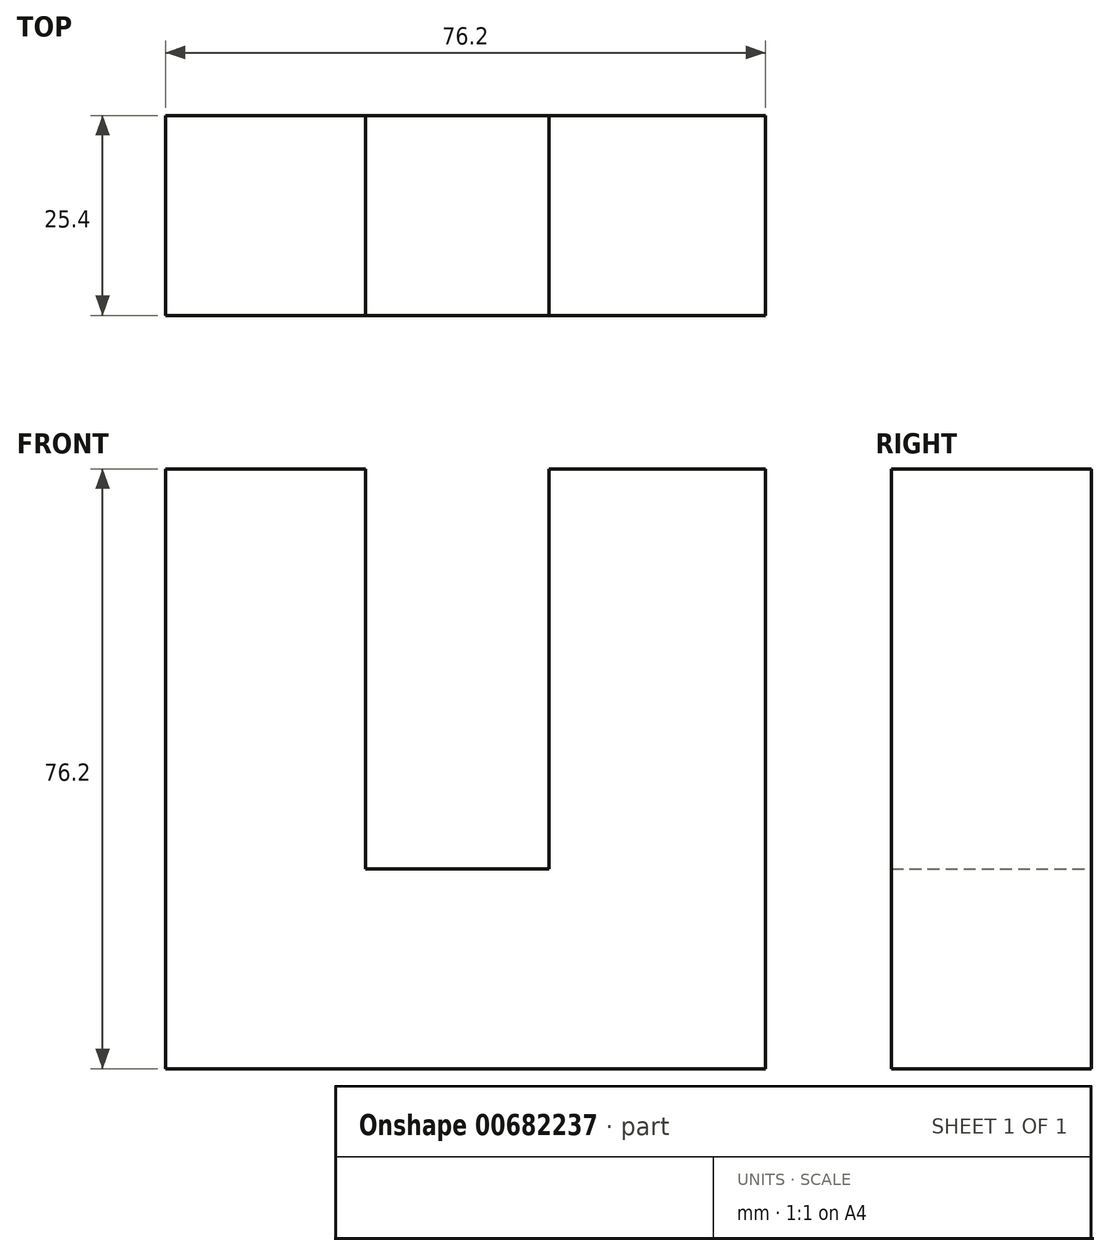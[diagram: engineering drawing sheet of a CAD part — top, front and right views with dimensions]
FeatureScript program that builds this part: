
annotation { "Feature Type Name" : "Feature", "Feature Type Description" : "" }
export const myFeature = defineFeature(function(context is Context, id is Id, definition is map)
    precondition{}
    {
        {
            var Q0;
            Q0=qCreatedBy(makeId("Front.planeOp"),FACE);
            var sketch = newSketch(context, id + "F0", { "sketchPlane" : qUnion([Q0])});
            skLineSegment(sketch, "E0", {"start": v(0, 0) * mm, "end": v(-76.2, 0) * mm});
            skLineSegment(sketch, "E1", {"start": v(-76.2, 0) * mm, "end": v(-76.2, 76.2) * mm});
            skLineSegment(sketch, "E2", {"start": v(-76.2, 76.2) * mm, "end": v(-50.8, 76.2) * mm});
            skLineSegment(sketch, "E3", {"start": v(-50.8, 76.2) * mm, "end": v(-50.8, 25.4) * mm});
            skLineSegment(sketch, "E4", {"start": v(-50.8, 25.4) * mm, "end": v(-27.49, 25.4) * mm});
            skLineSegment(sketch, "E5", {"start": v(-27.49, 25.4) * mm, "end": v(-27.49, 41.3) * mm});
            skLineSegment(sketch, "E6", {"start": v(-27.49, 41.3) * mm, "end": v(-27.49, 76.2) * mm});
            skLineSegment(sketch, "E7", {"start": v(-27.49, 76.2) * mm, "end": v(0, 76.2) * mm});
            skLineSegment(sketch, "E8", {"start": v(0, 76.2) * mm, "end": v(0, 0) * mm});
            skSolve(sketch);
        }
        {
            var Q0;
            Q0 = qSketchRegion(id + "F0", true);
            extrude(context, id + "F1", {"entities" : qUnion([Q0]), "depth" : 25.4 * mm, "offsetDistance" : 25.4 * mm});
        }
    });
